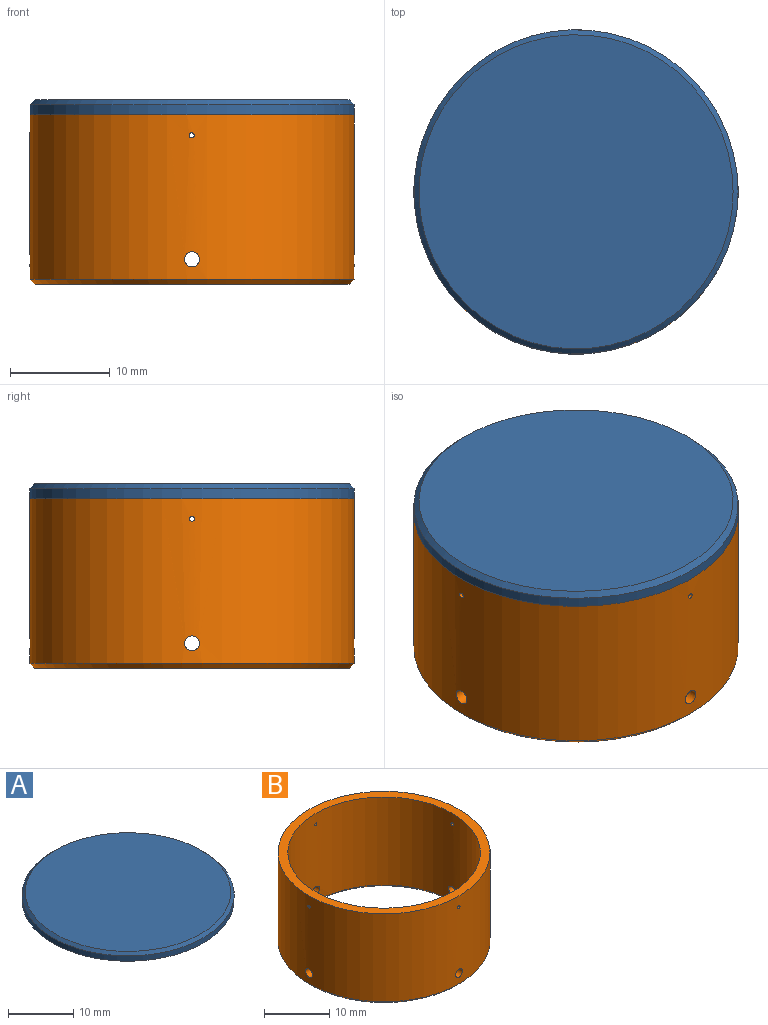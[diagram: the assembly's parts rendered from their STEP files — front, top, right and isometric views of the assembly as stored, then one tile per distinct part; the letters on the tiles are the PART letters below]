
ASSEMBLY  parts=2 mates=1
PART A: 4 faces, bbox 32.5x32.5x1.5 mm
  f0: cylinder r=16.25mm len=32.5mm, axis (0,0,-1), area 102.1mm2, adj f2,f3
  f1: plane 31.5x31.5mm, normal (0,0,1), area 779.3mm2, adj f3
  f2: plane 32.5x32.5mm, normal (0,0,-1), area 829.6mm2, adj f0
  f3: cone r=15.75mm half-angle=45deg, axis (0,0,-1), area 71.1mm2, adj f0,f1
PART B: 14 faces, bbox 32.5x32.5x17 mm
  f0: cylinder r=14.75mm len=29.5mm, axis (0,0,-1), area 1521.3mm2, adj f2,f4,f6,f7,f8,f9,f10,f11
  f1: cylinder r=16.25mm len=32.5mm, axis (0,0,-1), area 1676.8mm2, adj f2,f5,f6,f7,f8,f9,f10,f11
  f2: plane 32.5x32.5mm, normal (0,0,1), area 146.1mm2, adj f0,f1
  f3: plane 31.5x31.5mm, normal (0,0,-1), area 48.7mm2, adj f4,f5
  f4: cone r=15.25mm half-angle=45deg, axis (0,0,-1), area 66.6mm2, adj f0,f3
  f5: cone r=16.25mm half-angle=45deg, axis (0,0,1), area 71.1mm2, adj f1,f3
  f6: cylinder r=0.75mm len=1.52mm, axis (1,0,0), area 7.1mm2, adj f0,f1
  f7: cylinder r=0.75mm len=1.52mm, axis (1,0,0), area 7.1mm2, adj f0,f1
  f8: cylinder r=0.75mm len=1.52mm, axis (0,-1,0), area 7.1mm2, adj f0,f1
  f9: cylinder r=0.75mm len=1.52mm, axis (0,-1,0), area 7.1mm2, adj f0,f1
  f10: cylinder r=0.25mm len=1.5mm, axis (1,0,0), area 2.4mm2, adj f0,f1
  f11: cylinder r=0.25mm len=1.5mm, axis (1,0,0), area 2.4mm2, adj f0,f1
  f12: cylinder r=0.25mm len=1.5mm, axis (0,-1,0), area 2.4mm2, adj f0,f1
  f13: cylinder r=0.25mm len=1.5mm, axis (0,-1,0), area 2.4mm2, adj f0,f1
PLACE A rot(axis=(0,1,0),0deg) t=(-54.87,110.63,-9.44)mm
PLACE B rot(axis=(0,1,0),0deg) t=(-54.87,110.63,-26.44)mm
MATE fastened B.f0 <-> A.f0  axis (0,0,1) through (-54.87,110.63,-9.44)mm
